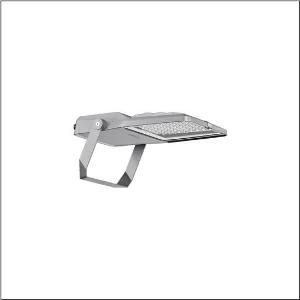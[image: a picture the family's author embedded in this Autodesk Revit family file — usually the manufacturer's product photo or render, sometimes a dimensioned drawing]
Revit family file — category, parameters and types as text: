
# Revit family: floodlight_fl_21_iq_mini___pl64_5xa7771d2e1a_0f9a
name_source: partatom
category: Lighting Fixtures
units: mm (PartAtom-declared; Revit-internal decimal feet)

## family parameters
Cut with Voids When Loaded = No
Host = Face
Light Source = No
Part Type = Normal
Room Calculation Point = No
Round Connector Dimension = Use Diameter
Shared = No

## types (1)
- --- (1 x LED, 17220 lm, 143 W, 3000K)
    Apparent Load = 143 VA
    CIE Flux Codes = 28 80 98 100 100
    Color Rendering = 70
    Color Temperature = 3000K
    Default Elevation = 1800 mm
    Description = Floodlight FL 21 iQ mini, floodlight, primary light control with lens, of PMMA, primary optical cover: protective disc, of toughened safety glass, transparent, light distribution: PL64, light emission: direct distribution, installation type: surface-mounted, LED, High Power LED, rated luminous flux: 17.220lm, luminous efficacy: 120lm/W, light colour: 730, colour temperature: 3000K, control: Auto-Match, Temp-Guard, Lumen-Switch, Night-Set, Smart-Wire, Light-Fading, Desk-Remote (wireless, voltage-free reading and setting of iQ features in the workshop via application-optimized NFC function/RFID function), optimised constant luminous flux control (CLO 2.0), with terminal, 6-pole, mains connection: 220..240V, AC, 50/60Hz, start of lifetime: 143W, end of service life: 152W, reduction: 61W, luminaire housing, of diecast aluminium, powder-coated, Siteco® metallic grey (DB 702S), corrosivity category C5 mid according to DIN EN ISO 12944, sealing non-destructively replaceable, mounting bracket, of steel, galvanised, powder-coated, Siteco® metallic grey (DB 702S), protection rating (complete): IP66, insulation class (complete): insulation class II (safety insulation), certification: CE, ENEC, VDE, protection symbol: D, impact resistance: IK08, permissible operating ambient temperature: -40..+40°C, permissible operating ambient temperature for outdoor applications: -40..+50°C, standard: DIN EN 12944, LABS conformity tested according to VDMA 24364:2018-05, packaging unit: 1 piece

Light Distribution: PL64
    Height = 70 mm
    Lamp = 1 x LED
    Lamp Light Flux = 17220 lm
    Lamp Power = 143 W
    Lamp count = 1
    Length = 485 mm
    Luminous efficacy = 120 lm/W
    Manufacturer = Siteco
    ModVariant = No
    Model = 5XA7771D2E1A
    Number of Poles = 1
    OnlyDefault = Yes
    Power Factor = 1
    Product Name = Floodlight FL 21 iQ mini | PL64
    Product group = floodlight | pylon annexe
    ProductGroupID = 6200
    Protection Class = Protection class II
    Protection Degree = IP 66
    RLX_Detail_Level = 1
    RLX_Emergency_Light_Flux = 0 lm
    RLX_Emergency_Type = 0
    RLX_Emergency_Type_DB = No
    RlxData = <blob elided: 96509 chars, md5=362f37ba>
    Socket = socket
    Standby Power = 0 W
    System Light Flux = 17220 lm
    System Power = 143 W
    Type Comments = factory setting: luminous flux: 100 % | dim-lin: 254 | 730 mA
    Type Image = l_1006845.jpg
    URL = http://relux.com
    VarID = @adj_098443
    Voltage = 0 V
    Weight = 0.00 kg
    Width = 337 mm

## geometry (parser evidence)
native form markers: Blend x4, Sweep x12
no freeform markers — native parametric forms only
